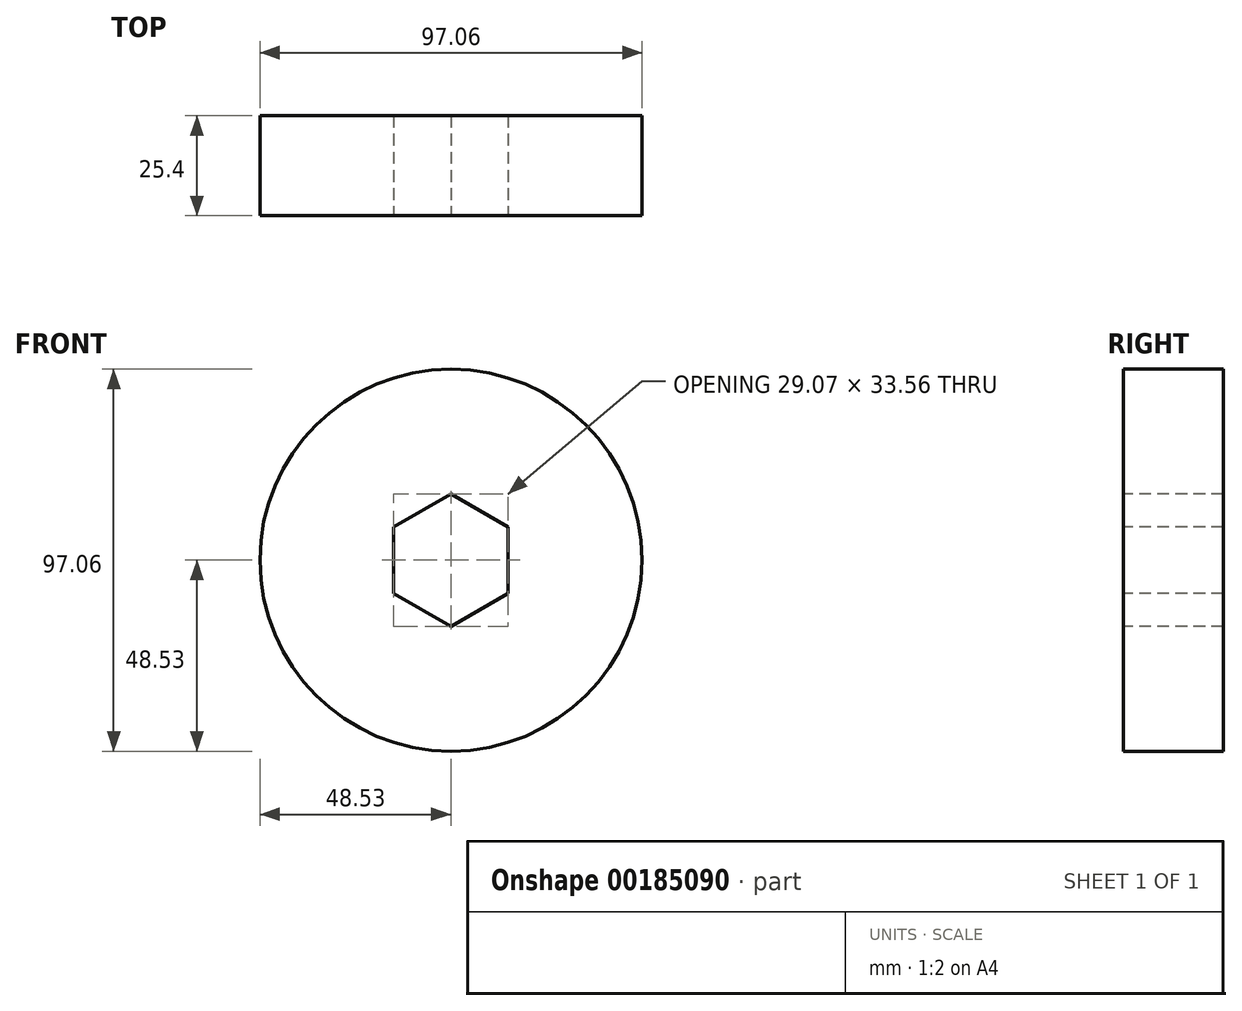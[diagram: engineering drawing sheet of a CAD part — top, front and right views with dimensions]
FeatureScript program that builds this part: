
annotation { "Feature Type Name" : "Feature", "Feature Type Description" : "" }
export const myFeature = defineFeature(function(context is Context, id is Id, definition is map)
    precondition{}
    {
        {
            var Q0;
            Q0=qCreatedBy(makeId("Front.planeOp"),FACE);
            var sketch = newSketch(context, id + "F0", { "sketchPlane" : qUnion([Q0])});
            skCircle(sketch, "E0", {"center": v(0, 0) * mm, "radius": 48.53 * mm});
            skSolve(sketch);
        }
        {
            var Q0;
            Q0=makeQuery(id+"F0.imprint","IMPRINT",FACE,{"disambiguationData":[TD([[makeQuery(id+"F0.imprint","IMPRINT",EDGE,{"derivedFrom":sQuery(id+"F0.wireOp",EDGE,"E0")}),1.0]])]});
            extrude(context, id + "F1", {"entities" : qUnion([Q0]), "endBound" : BoundingType.SYMMETRIC, "depth" : 25.4 * mm});
        }
        {
            var Q0;
            Q0=qCreatedBy(makeId("Front.planeOp"),FACE);
            var sketch = newSketch(context, id + "F2", { "sketchPlane" : qUnion([Q0])});
            skCircle(sketch, "E1.cCircle", {"center": v(0, 0) * mm, "radius": 16.78 * mm, "construction": true});
            skLineSegment(sketch, "E1.0", {"start": v(0, 16.78) * mm, "end": v(14.53, 8.4) * mm});
            skLineSegment(sketch, "E1.1", {"start": v(14.53, 8.4) * mm, "end": v(14.53, -8.4) * mm});
            skLineSegment(sketch, "E1.2", {"start": v(14.53, -8.4) * mm, "end": v(0, -16.78) * mm});
            skLineSegment(sketch, "E1.3", {"start": v(0, -16.78) * mm, "end": v(-14.53, -8.4) * mm});
            skLineSegment(sketch, "E1.4", {"start": v(-14.53, -8.4) * mm, "end": v(-14.53, 8.4) * mm});
            skLineSegment(sketch, "E1.5", {"start": v(-14.53, 8.4) * mm, "end": v(0, 16.78) * mm});
            skSolve(sketch);
        }
        {
            var Q0;
            Q0 = qSketchRegion(id + "F2", true);
            extrude(context, id + "F3", {"entities" : qUnion([Q0]), "operationType" : NewBodyOperationType.REMOVE, "endBound" : BoundingType.SYMMETRIC, "oppositeDirection" : true, "depth" : 25.4 * mm});
        }
    });
